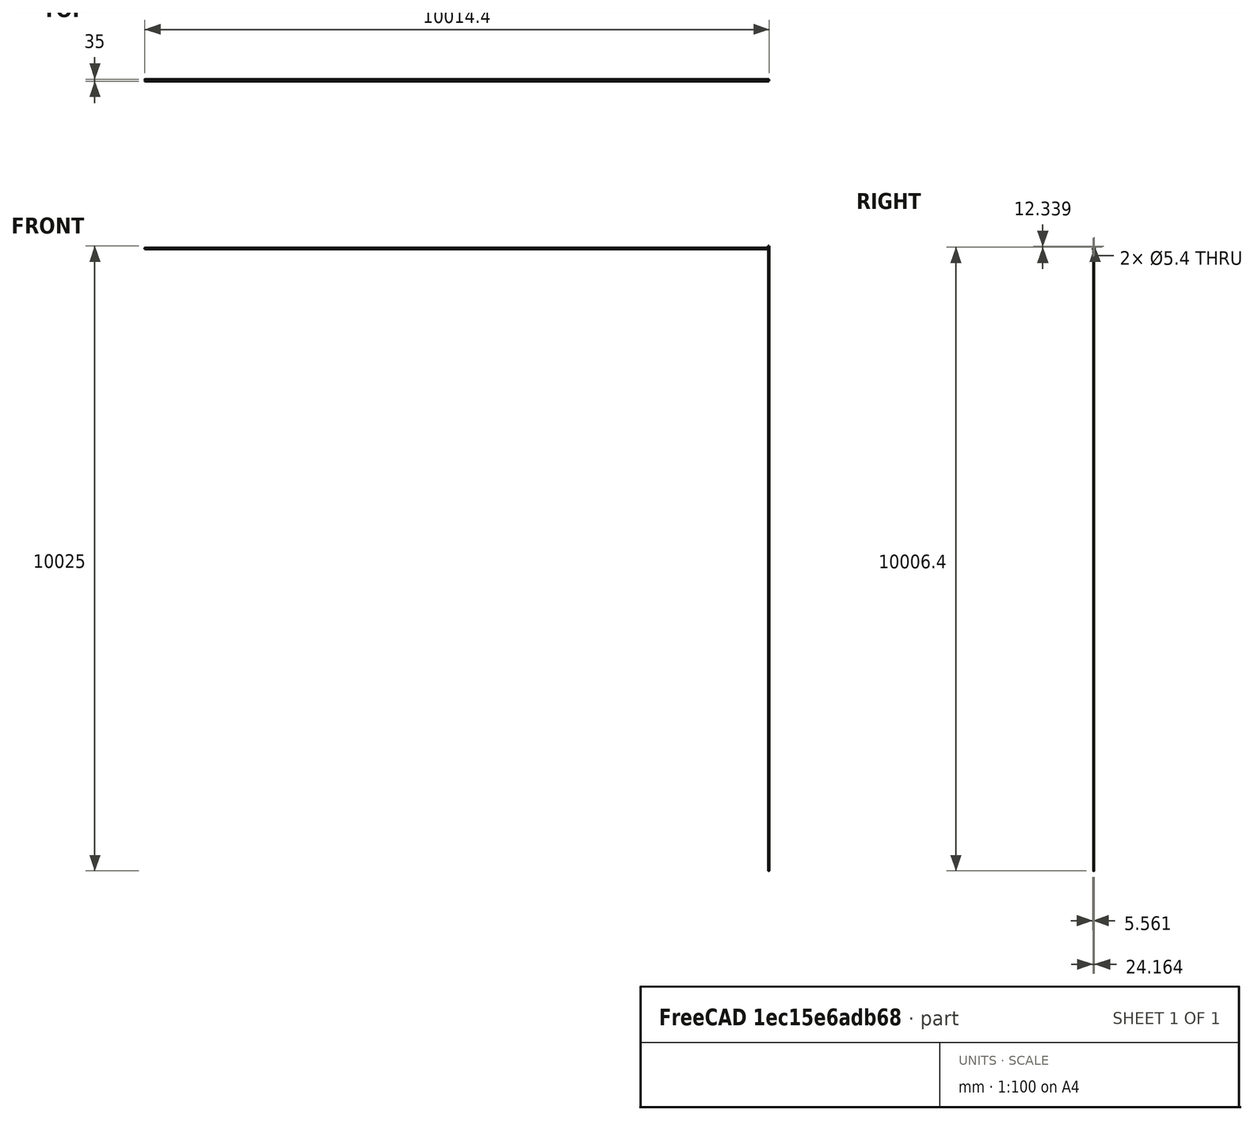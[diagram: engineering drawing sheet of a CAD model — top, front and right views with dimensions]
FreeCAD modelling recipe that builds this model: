
FCSTD DOCUMENT  (FreeCAD 0.16R)
Label: RackClip
License: All rights reserved
LicenseURL: http://en.wikipedia.org/wiki/All_rights_reserved
objects: Sketcher::SketchObject×6, PartDesign::Pocket×4, PartDesign::Fillet×3, PartDesign::Pad×2, Mesh::Feature×1
note: 21 computed .brp shape members not serialized (recipe doc carries the construction recipe); baked Part::Feature solids carry a one-line shape summary decoded from their .brp

FEATURE [Sketcher::SketchObject] Sketch002
  Placement = pos=(0,0,25) rot=(0,0,1;0rad)
  sketch-geometry (4):
    g0: LineSegment StartX=0 StartY=35 StartZ=0 EndX=5 EndY=35 EndZ=0
    g1: LineSegment StartX=5 StartY=35 StartZ=0 EndX=5 EndY=0 EndZ=0
    g2: LineSegment StartX=5 StartY=0 StartZ=0 EndX=0 EndY=0 EndZ=0
    g3: LineSegment StartX=0 StartY=0 StartZ=0 EndX=0 EndY=35 EndZ=0
  constraints (11):
    c: Coincident(g0,g1)
    c: Coincident(g1,g2)
    c: Coincident(g2,g3)
    c: Coincident(g3,g0)
    c: Horizontal(g0)
    c: Horizontal(g2)
    c: Vertical(g1)
    c: Vertical(g3)
    c: Distance(g2) = 5
    c: Distance(g1) = 35
    c: Coincident(g2,g-1)
FEATURE [PartDesign::Pad] Pad
  Length = 25
  Length2 = 100
  Placement = pos=(0,0,25) rot=(0,0,1;0rad)
  Sketch = -> Sketch002
  Type = 0
FEATURE [Sketcher::SketchObject] Sketch
  ExternalGeometry = -> [Pad]
  Placement = pos=(0,0,50) rot=(0,0,1;0rad)
  Support = -> Pad [Face6]
  sketch-geometry (1):
    g0: Circle CenterX=9.25 CenterY=17.8486 CenterZ=0 NormalX=0 NormalY=0 NormalZ=1 Radius=7
  constraints (2):
    c: Radius(g0) = 7
    c: DistanceX(g0) = 9.25
FEATURE [PartDesign::Pad] Pad001
  Length = 25
  Length2 = 100
  Placement = pos=(0,0,25) rot=(0,0,1;0rad)
  Reversed = true
  Sketch = -> Sketch
  Type = 0
FEATURE [Sketcher::SketchObject] Sketch003
  ExternalGeometry = -> [Pad001]
  Placement = pos=(0,0,50) rot=(0,0,1;0rad)
  Support = -> Pad001 [Face11]
  sketch-geometry (1):
    g0: Circle CenterX=9.24744 CenterY=17.643 CenterZ=0 NormalX=0 NormalY=0 NormalZ=1 Radius=4.2
  constraints (1):
    c: Radius(g0) = 4.2
FEATURE [PartDesign::Pocket] Pocket
  Length = 5
  Placement = pos=(0,0,25) rot=(0,0,1;0rad)
  Sketch = -> Sketch003
  Type = 1
FEATURE [Sketcher::SketchObject] Sketch004
  Placement = pos=(0,0,50) rot=(0,0,1;0rad)
  Support = -> Pocket [Face5]
  sketch-geometry (4):
    g0: LineSegment StartX=10.1031 StartY=20.6002 StartZ=0 EndX=19.4336 EndY=20.6002 EndZ=0
    g1: LineSegment StartX=19.4336 StartY=20.6002 StartZ=0 EndX=19.4336 EndY=14.6002 EndZ=0
    g2: LineSegment StartX=19.4336 StartY=14.6002 StartZ=0 EndX=10.1031 EndY=14.6002 EndZ=0
    g3: LineSegment StartX=10.1031 StartY=14.6002 StartZ=0 EndX=10.1031 EndY=20.6002 EndZ=0
  constraints (9):
    c: Coincident(g0,g1)
    c: Coincident(g1,g2)
    c: Coincident(g2,g3)
    c: Coincident(g3,g0)
    c: Horizontal(g0)
    c: Horizontal(g2)
    c: Vertical(g1)
    c: Vertical(g3)
    c: Distance(g3) = 6
FEATURE [PartDesign::Pocket] Pocket001
  Length = 5
  Placement = pos=(0,0,25) rot=(0,0,1;0rad)
  Sketch = -> Sketch004
  Type = 1
FEATURE [Sketcher::SketchObject] Sketch005
  Placement = pos=(5,0,25) rot=(0.57735,0.57735,0.57735;2.0944rad)
  Support = -> Pocket001 [Face3]
  sketch-geometry (2):
    g0: Circle CenterX=29.7252 CenterY=18.7423 CenterZ=0 NormalX=0 NormalY=0 NormalZ=1 Radius=2.7
    g1: Circle CenterX=5.56076 CenterY=6.40305 CenterZ=0 NormalX=0 NormalY=0 NormalZ=1 Radius=2.7
  constraints (2):
    c: Radius(g0) = 2.7
    c: Equal(g0,g1)
FEATURE [PartDesign::Pocket] Pocket002
  Length = 5
  Placement = pos=(0,0,25) rot=(0,0,1;0rad)
  Sketch = -> Sketch005
  Type = 1
FEATURE [Sketcher::SketchObject] Sketch006
  ExternalGeometry = -> [Pocket]
  Placement = pos=(5,0,25) rot=(0.57735,0.57735,0.57735;2.0944rad)
  Support = -> Pocket002 [Face3]
  sketch-geometry (14):
    g0: LineSegment StartX=9.78863 StartY=8.7817 StartZ=0 EndX=5.66363 EndY=11.1633 EndZ=0
    g1: LineSegment StartX=5.66363 StartY=11.1633 StartZ=0 EndX=1.53863 EndY=8.7817 EndZ=0
    g2: LineSegment StartX=1.53863 StartY=8.7817 StartZ=0 EndX=1.53863 EndY=4.01856 EndZ=0
    g3: LineSegment StartX=1.53863 StartY=4.01856 StartZ=0 EndX=5.66363 EndY=1.637 EndZ=0
    g4: LineSegment StartX=5.66363 StartY=1.637 StartZ=0 EndX=9.78863 EndY=4.01856 EndZ=0
    g5: LineSegment StartX=9.78863 StartY=4.01856 StartZ=0 EndX=9.78863 EndY=8.7817 EndZ=0
    g6: Circle [constr] CenterX=5.66363 CenterY=6.40013 CenterZ=0 NormalX=0 NormalY=0 NormalZ=1 Radius=4.76314
    g7: LineSegment StartX=29.8215 StartY=13.881 StartZ=0 EndX=33.9465 EndY=16.2626 EndZ=0
    g8: LineSegment StartX=33.9465 StartY=16.2626 StartZ=0 EndX=33.9465 EndY=21.0257 EndZ=0
    g9: LineSegment StartX=33.9465 StartY=21.0257 StartZ=0 EndX=29.8215 EndY=23.4073 EndZ=0
    g10: LineSegment StartX=29.8215 StartY=23.4073 StartZ=0 EndX=25.6965 EndY=21.0257 EndZ=0
    g11: LineSegment StartX=25.6965 StartY=21.0257 StartZ=0 EndX=25.6965 EndY=16.2626 EndZ=0
    g12: LineSegment StartX=25.6965 StartY=16.2626 StartZ=0 EndX=29.8215 EndY=13.881 EndZ=0
    g13: Circle [constr] CenterX=29.8215 CenterY=18.6442 CenterZ=0 NormalX=0 NormalY=0 NormalZ=1 Radius=4.76314
  constraints (30):
    c: Coincident(g0,g1)
    c: Coincident(g1,g2)
    c: Coincident(g2,g3)
    c: Coincident(g3,g4)
    c: Coincident(g4,g5)
    c: Coincident(g5,g0)
    c: Equal(g0, g1-g5) x5
    c: PointOnObject(g0,g6)
    c: PointOnObject(g1,g6)
    c: PointOnObject(g2,g6)
    c: PointOnObject(g3,g6)
    c: PointOnObject(g4,g6)
    c: PointOnObject(g5,g6)
    c: Distance(g0,g1) = 8.25
    c: Coincident(g7,g8)
    c: Coincident(g8,g9)
    c: Coincident(g9,g10)
    c: Coincident(g10,g11)
    c: Coincident(g11,g12)
    c: Coincident(g12,g7)
    c: Equal(g7, g8-g12) x5
    c: PointOnObject(g7,g13)
    c: PointOnObject(g8,g13)
    c: PointOnObject(g9,g13)
    c: PointOnObject(g10,g13)
    c: PointOnObject(g11,g13)
    c: PointOnObject(g12,g13)
    c: Distance(g7,g8) = 8.25
    c: Vertical(g8)
    c: Vertical(g5)
FEATURE [PartDesign::Pocket] Pocket003
  Length = 2
  Placement = pos=(0,0,25) rot=(0,0,1;0rad)
  Sketch = -> Sketch006
  Type = 0
FEATURE [PartDesign::Fillet] Fillet
  Base = -> Pocket003 [Edge5,Edge32,Edge69,Edge1]
  Placement = pos=(0,0,25) rot=(0,0,1;0rad)
  Radius = 1
FEATURE [PartDesign::Fillet] Fillet001
  Base = -> Fillet [Edge32,Edge14]
  Placement = pos=(0,0,25) rot=(0,0,1;0rad)
  Radius = 1
FEATURE [PartDesign::Fillet] Fillet002
  Base = -> Fillet001 [Edge39,Edge12]
  Placement = pos=(0,0,25) rot=(0,0,1;0rad)
  Radius = 1
FEATURE [Mesh::Feature] Mesh  label="Fillet002 (Meshed)"
